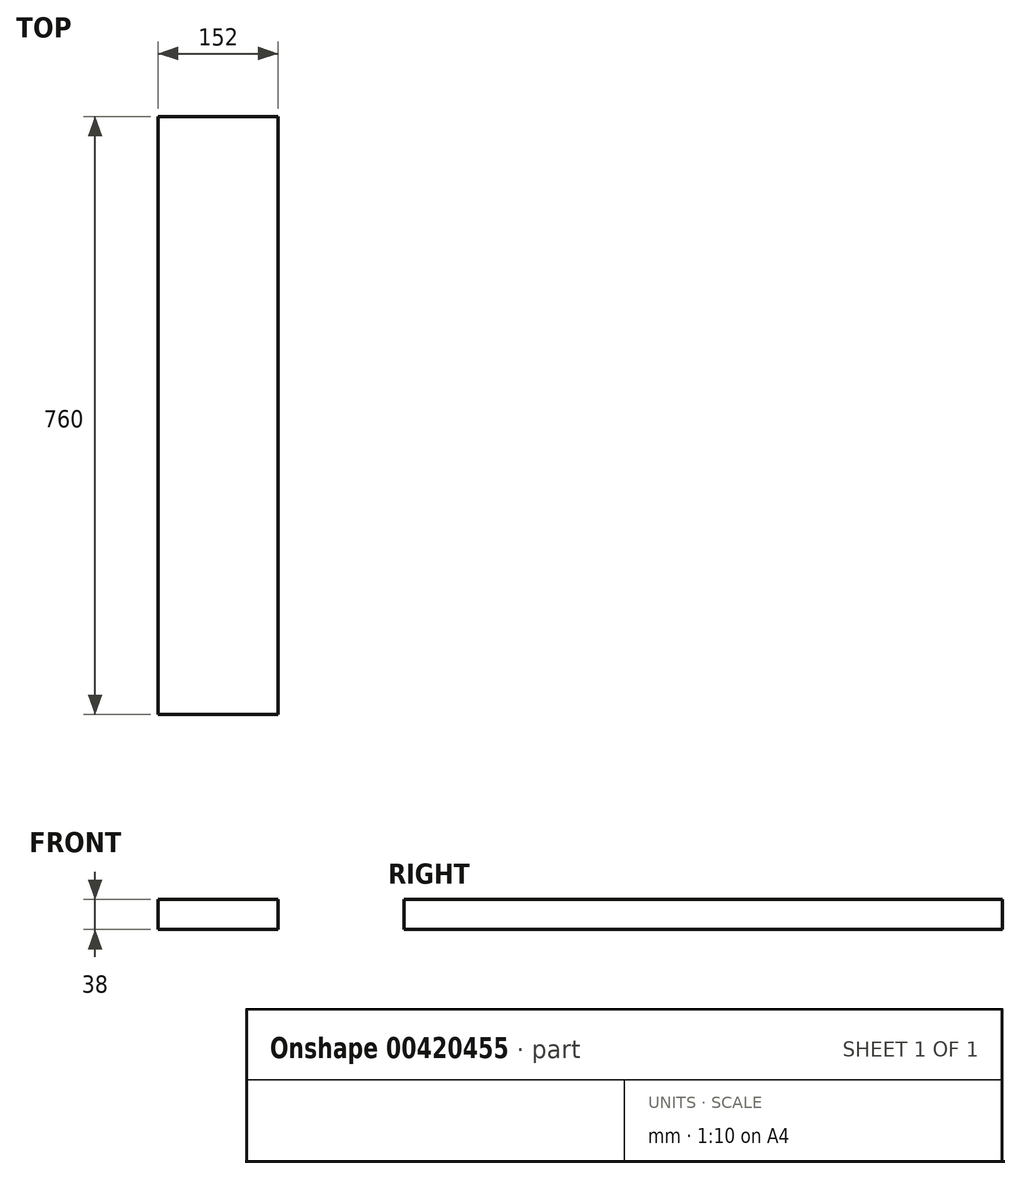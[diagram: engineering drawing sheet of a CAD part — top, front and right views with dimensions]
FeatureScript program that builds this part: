
annotation { "Feature Type Name" : "Feature", "Feature Type Description" : "" }
export const myFeature = defineFeature(function(context is Context, id is Id, definition is map)
    precondition{}
    {
        {
            var Q0;
            Q0=qCreatedBy(makeId("Front.planeOp"),FACE);
            var sketch = newSketch(context, id + "F0", { "sketchPlane" : qUnion([Q0])});
            skLineSegment(sketch, "E0.bottom", {"start": v(76, 19) * mm, "end": v(-76, 19) * mm});
            skLineSegment(sketch, "E0.top", {"start": v(76, -19) * mm, "end": v(-76, -19) * mm});
            skLineSegment(sketch, "E0.left", {"start": v(76, 19) * mm, "end": v(76, -19) * mm});
            skLineSegment(sketch, "E0.right", {"start": v(-76, 19) * mm, "end": v(-76, -19) * mm});
            skPoint(sketch, "E0.middle", {"position": v(0, 0) * mm});
            skSolve(sketch);
        }
        {
            var Q0;
            Q0=makeQuery(id+"F0.imprint","IMPRINT",FACE,{"disambiguationData":[TD([[makeQuery(id+"F0.imprint","IMPRINT",EDGE,{"derivedFrom":sQuery(id+"F0.wireOp",EDGE,"E0.bottom")}),1.0]])]});
            extrude(context, id + "F1", {"entities" : qUnion([Q0]), "endBound" : BoundingType.SYMMETRIC, "depth" : 760 * mm});
        }
    });
